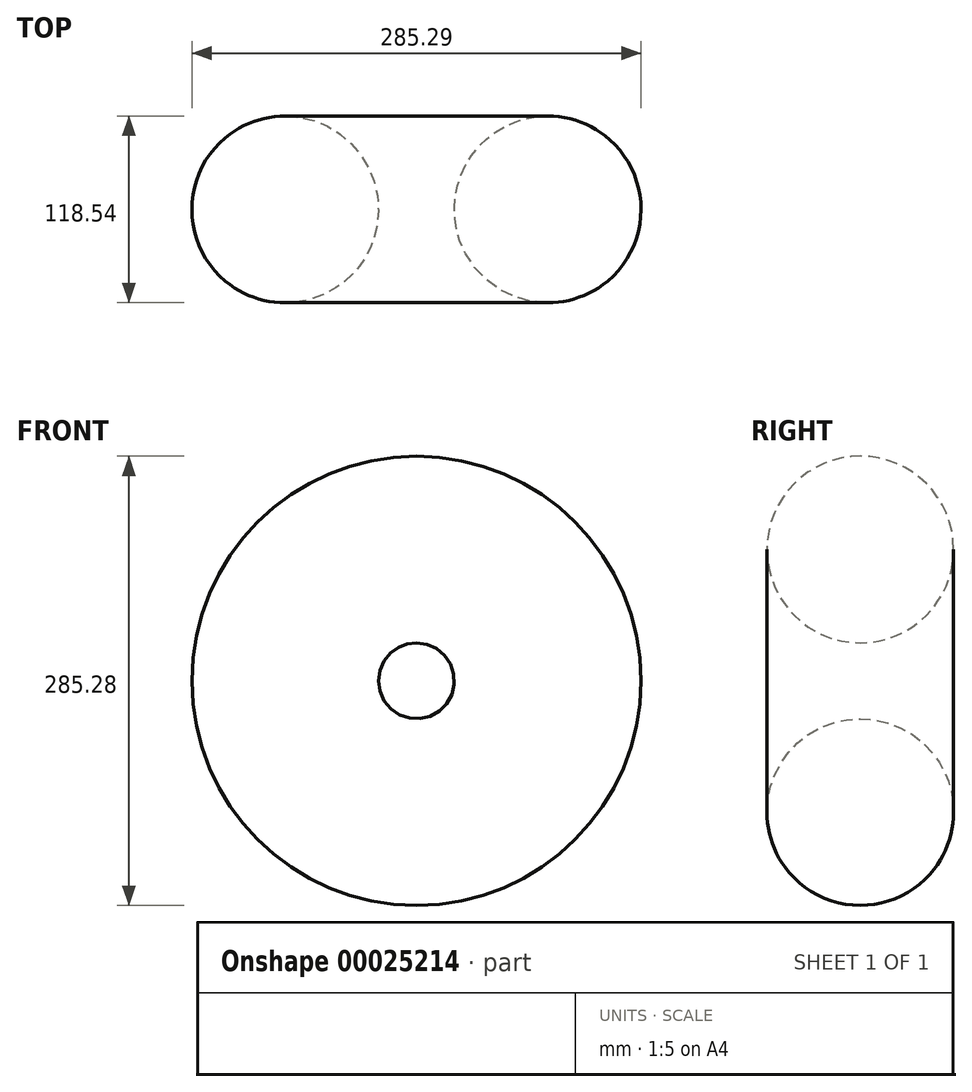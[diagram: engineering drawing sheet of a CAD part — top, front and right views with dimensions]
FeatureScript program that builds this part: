
annotation { "Feature Type Name" : "Feature", "Feature Type Description" : "" }
export const myFeature = defineFeature(function(context is Context, id is Id, definition is map)
    precondition{}
    {
        {
            var Q0;
            Q0=qCreatedBy(makeId("Top.planeOp"),FACE);
            var sketch = newSketch(context, id + "F0", { "sketchPlane" : qUnion([Q0])});
            skLineSegment(sketch, "E0", {"start": v(-83.38, 66.75) * mm, "end": v(-83.38, -63.63) * mm});
            skCircle(sketch, "E1", {"center": v(0, 0) * mm, "radius": 59.27 * mm});
            skSolve(sketch);
        }
        {
            var Q0;
            Q0=makeQuery(id+"F0.imprint","IMPRINT",FACE,{"disambiguationData":[TD([[makeQuery(id+"F0.imprint","IMPRINT",EDGE,{"derivedFrom":sQuery(id+"F0.wireOp",EDGE,"E1")}),1.0]])]});
            var Q1;
            Q1=sQuery(id+"F0.wireOp",EDGE,"E0");
            revolve(context, id + "F1", {"entities" : qUnion([Q0]), "axis" : qUnion([Q1]), "revolveType" : RevolveType.FULL});
        }
        {
            var Q0;
            Q0=qCreatedBy(makeId("Front.planeOp"),FACE);
            var sketch = newSketch(context, id + "F2", { "sketchPlane" : qUnion([Q0])});
            skCircle(sketch, "E2", {"center": v(-77.42, 97.4) * mm, "radius": 14.27 * mm});
            skCircle(sketch, "E3", {"center": v(-89.57, -73.1) * mm, "radius": 18.56 * mm});
            skSolve(sketch);
        }
        {
            var Q0;
            Q0=sQuery(id+"F2.wireOp",EDGE,"E2");
            var Q1;
            Q1=sQuery(id+"F2.wireOp",EDGE,"E3");
            extrude(context, id + "F3", {"bodyType" : ToolBodyType.SURFACE, "surfaceEntities" : qUnion([Q0, Q1]), "depth" : 25.4 * mm});
        }
    });
